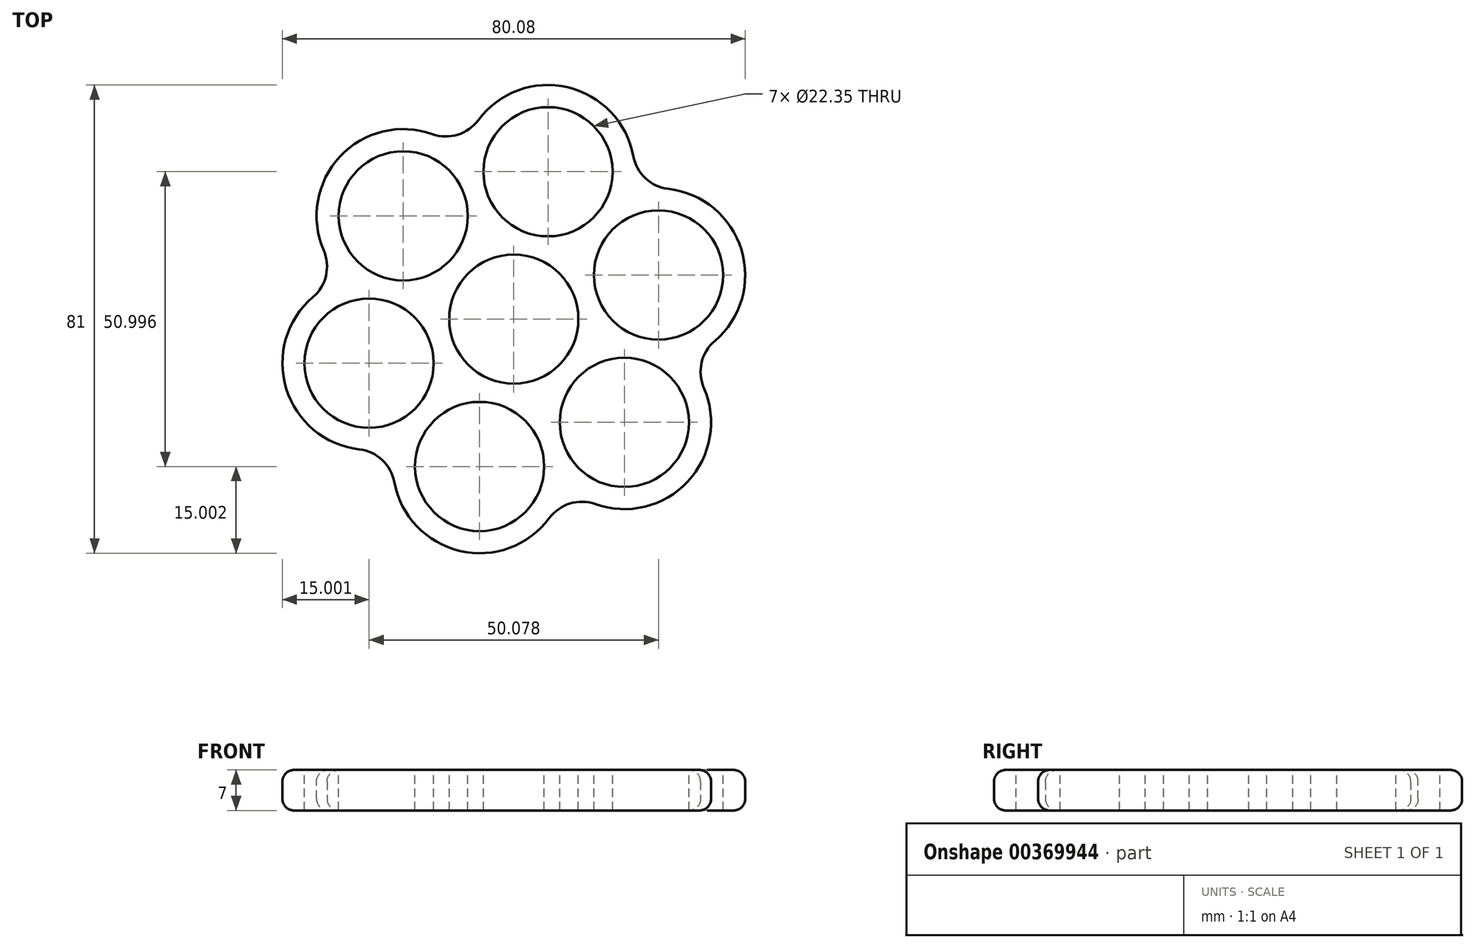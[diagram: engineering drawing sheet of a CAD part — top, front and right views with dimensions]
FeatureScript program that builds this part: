
annotation { "Feature Type Name" : "Feature", "Feature Type Description" : "" }
export const myFeature = defineFeature(function(context is Context, id is Id, definition is map)
    precondition{}
    {
        {
            var Q0;
            Q0=qCreatedBy(makeId("Top.planeOp"),FACE);
            var sketch = newSketch(context, id + "F0", { "sketchPlane" : qUnion([Q0])});
            skCircle(sketch, "E0", {"center": v(0, 0) * mm, "radius": 11.18 * mm});
            skLineSegment(sketch, "E1", {"start": v(0, 0) * mm, "end": v(-19.13, 17.87) * mm});
            skLineSegment(sketch, "E2", {"start": v(0, 0) * mm, "end": v(25.04, 7.63) * mm});
            skLineSegment(sketch, "E3", {"start": v(0, 0) * mm, "end": v(-5.91, -25.5) * mm});
            skCircle(sketch, "E4", {"center": v(-19.13, 17.87) * mm, "radius": 11.18 * mm});
            skCircle(sketch, "E5", {"center": v(25.04, 7.63) * mm, "radius": 11.18 * mm});
            skCircle(sketch, "E6", {"center": v(-5.91, -25.5) * mm, "radius": 11.18 * mm});
            skCircle(sketch, "E7", {"center": v(0, 0) * mm, "radius": 15 * mm});
            skCircle(sketch, "E8", {"center": v(-19.13, 17.87) * mm, "radius": 15 * mm});
            skCircle(sketch, "E9", {"center": v(25.04, 7.63) * mm, "radius": 15 * mm});
            skCircle(sketch, "E10", {"center": v(-5.91, -25.5) * mm, "radius": 15 * mm});
            skLineSegment(sketch, "E11", {"start": v(-19.13, 17.87) * mm, "end": v(-8.88, 28.83) * mm});
            skLineSegment(sketch, "E12", {"start": v(25.04, 7.63) * mm, "end": v(20.67, 21.98) * mm});
            skLineSegment(sketch, "E13", {"start": v(-5.91, -25.5) * mm, "end": v(8.7, -28.89) * mm});
            skLineSegment(sketch, "E14", {"start": v(-5.91, -25.5) * mm, "end": v(-20.53, -22.1) * mm});
            skLineSegment(sketch, "E15", {"start": v(-19.13, 17.87) * mm, "end": v(-29.37, 6.91) * mm});
            skLineSegment(sketch, "E16", {"start": v(25.04, 7.63) * mm, "end": v(29.41, -6.72) * mm});
            skLineSegment(sketch, "E17", {"start": v(0, 0) * mm, "end": v(5.91, 25.5) * mm});
            skLineSegment(sketch, "E18", {"start": v(0, 0) * mm, "end": v(19.13, -17.87) * mm});
            skLineSegment(sketch, "E19", {"start": v(0, 0) * mm, "end": v(-25.04, -7.63) * mm});
            skCircle(sketch, "E20", {"center": v(-25.04, -7.63) * mm, "radius": 11.18 * mm});
            skCircle(sketch, "E21", {"center": v(5.91, 25.5) * mm, "radius": 11.18 * mm});
            skCircle(sketch, "E22", {"center": v(19.13, -17.87) * mm, "radius": 11.18 * mm});
            skCircle(sketch, "E23", {"center": v(-25.04, -7.63) * mm, "radius": 15 * mm});
            skCircle(sketch, "E24", {"center": v(5.91, 25.5) * mm, "radius": 15 * mm});
            skCircle(sketch, "E25", {"center": v(19.13, -17.87) * mm, "radius": 15 * mm});
            skSolve(sketch);
        }
        {
            var Q0;
            {var subQ0=sQuery(id+"F0.wireOp",EDGE,"E11");var subQ1=sQuery(id+"F0.wireOp",EDGE,"E4");var subQ2=makeQuery(id+"F0.imprint","INTERSECT",VERTEX,{"derivedFrom":[subQ1,subQ0]});Q0=makeQuery(id+"F0.imprint","IMPRINT",FACE,{"disambiguationData":[TD([[makeQuery(id+"F0.imprint","IMPRINT",EDGE,{"disambiguationData":[TD([[subQ2,1.0]])],"derivedFrom":subQ1}),-1.0]])]});}
            var Q1;
            {var subQ0=sQuery(id+"F0.wireOp",EDGE,"E11");var subQ1=sQuery(id+"F0.wireOp",EDGE,"E4");var subQ2=makeQuery(id+"F0.imprint","INTERSECT",VERTEX,{"derivedFrom":[subQ1,subQ0]});Q1=makeQuery(id+"F0.imprint","IMPRINT",FACE,{"disambiguationData":[TD([[makeQuery(id+"F0.imprint","IMPRINT",EDGE,{"disambiguationData":[TD([[subQ2,-1.0]])],"derivedFrom":subQ1}),-1.0]])]});}
            var Q2;
            {var subQ0=sQuery(id+"F0.wireOp",EDGE,"E15");var subQ1=sQuery(id+"F0.wireOp",EDGE,"E4");var subQ2=makeQuery(id+"F0.imprint","INTERSECT",VERTEX,{"derivedFrom":[subQ1,subQ0]});Q2=makeQuery(id+"F0.imprint","IMPRINT",FACE,{"disambiguationData":[TD([[makeQuery(id+"F0.imprint","IMPRINT",EDGE,{"disambiguationData":[TD([[subQ2,-1.0]])],"derivedFrom":subQ1}),-1.0]])]});}
            var Q3;
            {var subQ0=sQuery(id+"F0.wireOp",EDGE,"E24");var subQ1=sQuery(id+"F0.wireOp",EDGE,"E5");var subQ2=makeQuery(id+"F0.imprint","INTERSECT",VERTEX,{"derivedFrom":[subQ1,subQ0]});Q3=makeQuery(id+"F0.imprint","IMPRINT",FACE,{"disambiguationData":[TD([[makeQuery(id+"F0.imprint","IMPRINT",EDGE,{"disambiguationData":[TD([[subQ2,1.0]])],"derivedFrom":subQ1}),-1.0]])]});}
            var Q4;
            {var subQ0=sQuery(id+"F0.wireOp",EDGE,"E25");var subQ1=sQuery(id+"F0.wireOp",EDGE,"E5");var subQ2=makeQuery(id+"F0.imprint","INTERSECT",VERTEX,{"derivedFrom":[subQ1,subQ0]});Q4=makeQuery(id+"F0.imprint","IMPRINT",FACE,{"disambiguationData":[TD([[makeQuery(id+"F0.imprint","IMPRINT",EDGE,{"disambiguationData":[TD([[subQ2,-1.0]])],"derivedFrom":subQ1}),-1.0]])]});}
            var Q5;
            {var subQ0=sQuery(id+"F0.wireOp",EDGE,"E12");var subQ1=sQuery(id+"F0.wireOp",EDGE,"E5");var subQ2=makeQuery(id+"F0.imprint","INTERSECT",VERTEX,{"derivedFrom":[subQ1,subQ0]});Q5=makeQuery(id+"F0.imprint","IMPRINT",FACE,{"disambiguationData":[TD([[makeQuery(id+"F0.imprint","IMPRINT",EDGE,{"disambiguationData":[TD([[subQ2,1.0]])],"derivedFrom":subQ1}),-1.0]])]});}
            var Q6;
            {var subQ0=sQuery(id+"F0.wireOp",EDGE,"E23");var subQ1=sQuery(id+"F0.wireOp",EDGE,"E6");var subQ2=makeQuery(id+"F0.imprint","INTERSECT",VERTEX,{"derivedFrom":[subQ1,subQ0]});Q6=makeQuery(id+"F0.imprint","IMPRINT",FACE,{"disambiguationData":[TD([[makeQuery(id+"F0.imprint","IMPRINT",EDGE,{"disambiguationData":[TD([[subQ2,-1.0]])],"derivedFrom":subQ1}),-1.0]])]});}
            var Q7;
            {var subQ0=sQuery(id+"F0.wireOp",EDGE,"E14");var subQ1=sQuery(id+"F0.wireOp",EDGE,"E6");var subQ2=makeQuery(id+"F0.imprint","INTERSECT",VERTEX,{"derivedFrom":[subQ1,subQ0]});Q7=makeQuery(id+"F0.imprint","IMPRINT",FACE,{"disambiguationData":[TD([[makeQuery(id+"F0.imprint","IMPRINT",EDGE,{"disambiguationData":[TD([[subQ2,-1.0]])],"derivedFrom":subQ1}),-1.0]])]});}
            var Q8;
            {var subQ0=sQuery(id+"F0.wireOp",EDGE,"E25");var subQ1=sQuery(id+"F0.wireOp",EDGE,"E6");var subQ2=makeQuery(id+"F0.imprint","INTERSECT",VERTEX,{"derivedFrom":[subQ1,subQ0]});Q8=makeQuery(id+"F0.imprint","IMPRINT",FACE,{"disambiguationData":[TD([[makeQuery(id+"F0.imprint","IMPRINT",EDGE,{"disambiguationData":[TD([[subQ2,1.0]])],"derivedFrom":subQ1}),-1.0]])]});}
            var Q9;
            {var subQ0=sQuery(id+"F0.wireOp",EDGE,"E24");var subQ1=sQuery(id+"F0.wireOp",EDGE,"E8");var subQ2=makeQuery(id+"F0.imprint","INTERSECT",VERTEX,{"disambiguationData":[OD(0.0)],"derivedFrom":[subQ1,subQ0]});Q9=makeQuery(id+"F0.imprint","IMPRINT",FACE,{"disambiguationData":[TD([[makeQuery(id+"F0.imprint","IMPRINT",EDGE,{"disambiguationData":[TD([[subQ2,1.0]])],"derivedFrom":subQ1}),-1.0]])]});}
            var Q10;
            {var subQ0=sQuery(id+"F0.wireOp",EDGE,"E23");var subQ1=sQuery(id+"F0.wireOp",EDGE,"E8");var subQ2=makeQuery(id+"F0.imprint","INTERSECT",VERTEX,{"disambiguationData":[OD(0.0)],"derivedFrom":[subQ1,subQ0]});Q10=makeQuery(id+"F0.imprint","IMPRINT",FACE,{"disambiguationData":[TD([[makeQuery(id+"F0.imprint","IMPRINT",EDGE,{"disambiguationData":[TD([[subQ2,-1.0]])],"derivedFrom":subQ1}),-1.0]])]});}
            var Q11;
            {var subQ0=sQuery(id+"F0.wireOp",EDGE,"E25");var subQ1=sQuery(id+"F0.wireOp",EDGE,"E9");var subQ2=makeQuery(id+"F0.imprint","INTERSECT",VERTEX,{"disambiguationData":[OD(0.0)],"derivedFrom":[subQ1,subQ0]});Q11=makeQuery(id+"F0.imprint","IMPRINT",FACE,{"disambiguationData":[TD([[makeQuery(id+"F0.imprint","IMPRINT",EDGE,{"disambiguationData":[TD([[subQ2,1.0]])],"derivedFrom":subQ1}),-1.0]])]});}
            var Q12;
            {var subQ0=sQuery(id+"F0.wireOp",EDGE,"E24");var subQ1=sQuery(id+"F0.wireOp",EDGE,"E8");var subQ2=makeQuery(id+"F0.imprint","INTERSECT",VERTEX,{"disambiguationData":[OD(0.0)],"derivedFrom":[subQ1,subQ0]});Q12=makeQuery(id+"F0.imprint","IMPRINT",FACE,{"disambiguationData":[TD([[makeQuery(id+"F0.imprint","IMPRINT",EDGE,{"disambiguationData":[TD([[subQ2,1.0]])],"derivedFrom":subQ1}),1.0]])]});}
            var Q13;
            {var subQ0=sQuery(id+"F0.wireOp",EDGE,"E23");var subQ1=sQuery(id+"F0.wireOp",EDGE,"E8");var subQ2=makeQuery(id+"F0.imprint","INTERSECT",VERTEX,{"disambiguationData":[OD(0.0)],"derivedFrom":[subQ1,subQ0]});Q13=makeQuery(id+"F0.imprint","IMPRINT",FACE,{"disambiguationData":[TD([[makeQuery(id+"F0.imprint","IMPRINT",EDGE,{"disambiguationData":[TD([[subQ2,-1.0]])],"derivedFrom":subQ1}),1.0]])]});}
            var Q14;
            {var subQ0=sQuery(id+"F0.wireOp",EDGE,"E24");var subQ1=sQuery(id+"F0.wireOp",EDGE,"E9");var subQ2=makeQuery(id+"F0.imprint","INTERSECT",VERTEX,{"disambiguationData":[OD(0.0)],"derivedFrom":[subQ1,subQ0]});Q14=makeQuery(id+"F0.imprint","IMPRINT",FACE,{"disambiguationData":[TD([[makeQuery(id+"F0.imprint","IMPRINT",EDGE,{"disambiguationData":[TD([[subQ2,-1.0]])],"derivedFrom":subQ1}),1.0]])]});}
            var Q15;
            {var subQ0=sQuery(id+"F0.wireOp",EDGE,"E25");var subQ1=sQuery(id+"F0.wireOp",EDGE,"E9");var subQ2=makeQuery(id+"F0.imprint","INTERSECT",VERTEX,{"disambiguationData":[OD(1.0)],"derivedFrom":[subQ1,subQ0]});Q15=makeQuery(id+"F0.imprint","IMPRINT",FACE,{"disambiguationData":[TD([[makeQuery(id+"F0.imprint","IMPRINT",EDGE,{"disambiguationData":[TD([[subQ2,-1.0]])],"derivedFrom":subQ1}),1.0]])]});}
            var Q16;
            {var subQ0=sQuery(id+"F0.wireOp",EDGE,"E25");var subQ1=sQuery(id+"F0.wireOp",EDGE,"E10");var subQ2=makeQuery(id+"F0.imprint","INTERSECT",VERTEX,{"disambiguationData":[OD(1.0)],"derivedFrom":[subQ1,subQ0]});Q16=makeQuery(id+"F0.imprint","IMPRINT",FACE,{"disambiguationData":[TD([[makeQuery(id+"F0.imprint","IMPRINT",EDGE,{"disambiguationData":[TD([[subQ2,1.0]])],"derivedFrom":subQ1}),1.0]])]});}
            var Q17;
            {var subQ0=sQuery(id+"F0.wireOp",EDGE,"E23");var subQ1=sQuery(id+"F0.wireOp",EDGE,"E10");var subQ2=makeQuery(id+"F0.imprint","INTERSECT",VERTEX,{"disambiguationData":[OD(1.0)],"derivedFrom":[subQ1,subQ0]});Q17=makeQuery(id+"F0.imprint","IMPRINT",FACE,{"disambiguationData":[TD([[makeQuery(id+"F0.imprint","IMPRINT",EDGE,{"disambiguationData":[TD([[subQ2,-1.0]])],"derivedFrom":subQ1}),1.0]])]});}
            var Q18;
            {var subQ3=sQuery(id+"F0.wireOp",EDGE,"E7");var subQ5=sQuery(id+"F0.wireOp",EDGE,"E8");var subQ6=makeQuery(id+"F0.imprint","INTERSECT",VERTEX,{"disambiguationData":[OD(0.0)],"derivedFrom":[subQ3,subQ5]});Q18=makeQuery(id+"F0.imprint","IMPRINT",FACE,{"disambiguationData":[TD([[makeQuery(id+"F0.imprint","IMPRINT",EDGE,{"disambiguationData":[TD([[subQ6,-1.0]])],"derivedFrom":subQ5}),1.0]])]});}
            var Q19;
            {var subQ0=sQuery(id+"F0.wireOp",EDGE,"E8");var subQ3=sQuery(id+"F0.wireOp",EDGE,"E7");var subQ5=makeQuery(id+"F0.imprint","INTERSECT",VERTEX,{"disambiguationData":[OD(1.0)],"derivedFrom":[subQ3,subQ0]});Q19=makeQuery(id+"F0.imprint","IMPRINT",FACE,{"disambiguationData":[TD([[makeQuery(id+"F0.imprint","IMPRINT",EDGE,{"disambiguationData":[TD([[subQ5,1.0]])],"derivedFrom":subQ3}),1.0]])]});}
            var Q20;
            {var subQ3=sQuery(id+"F0.wireOp",EDGE,"E7");var subQ5=sQuery(id+"F0.wireOp",EDGE,"E8");var subQ6=makeQuery(id+"F0.imprint","INTERSECT",VERTEX,{"disambiguationData":[OD(1.0)],"derivedFrom":[subQ3,subQ5]});Q20=makeQuery(id+"F0.imprint","IMPRINT",FACE,{"disambiguationData":[TD([[makeQuery(id+"F0.imprint","IMPRINT",EDGE,{"disambiguationData":[TD([[subQ6,1.0]])],"derivedFrom":subQ5}),1.0]])]});}
            var Q21;
            {var subQ0=sQuery(id+"F0.wireOp",EDGE,"E8");var subQ3=sQuery(id+"F0.wireOp",EDGE,"E7");var subQ5=makeQuery(id+"F0.imprint","INTERSECT",VERTEX,{"disambiguationData":[OD(0.0)],"derivedFrom":[subQ3,subQ0]});Q21=makeQuery(id+"F0.imprint","IMPRINT",FACE,{"disambiguationData":[TD([[makeQuery(id+"F0.imprint","IMPRINT",EDGE,{"disambiguationData":[TD([[subQ5,-1.0]])],"derivedFrom":subQ3}),1.0]])]});}
            var Q22;
            {var subQ3=sQuery(id+"F0.wireOp",EDGE,"E21");var subQ5=sQuery(id+"F0.wireOp",EDGE,"E8");var subQ6=makeQuery(id+"F0.imprint","INTERSECT",VERTEX,{"derivedFrom":[subQ5,subQ3]});Q22=makeQuery(id+"F0.imprint","IMPRINT",FACE,{"disambiguationData":[TD([[makeQuery(id+"F0.imprint","IMPRINT",EDGE,{"disambiguationData":[TD([[subQ6,1.0]])],"derivedFrom":subQ5}),-1.0]])]});}
            var Q23;
            {var subQ0=sQuery(id+"F0.wireOp",EDGE,"E24");var subQ1=sQuery(id+"F0.wireOp",EDGE,"E7");var subQ2=makeQuery(id+"F0.imprint","INTERSECT",VERTEX,{"disambiguationData":[OD(1.0)],"derivedFrom":[subQ1,subQ0]});Q23=makeQuery(id+"F0.imprint","IMPRINT",FACE,{"disambiguationData":[TD([[makeQuery(id+"F0.imprint","IMPRINT",EDGE,{"disambiguationData":[TD([[subQ2,1.0]])],"derivedFrom":subQ1}),1.0]])]});}
            var Q24;
            {var subQ0=sQuery(id+"F0.wireOp",EDGE,"E24");var subQ1=sQuery(id+"F0.wireOp",EDGE,"E7");var subQ2=makeQuery(id+"F0.imprint","INTERSECT",VERTEX,{"disambiguationData":[OD(0.0)],"derivedFrom":[subQ1,subQ0]});Q24=makeQuery(id+"F0.imprint","IMPRINT",FACE,{"disambiguationData":[TD([[makeQuery(id+"F0.imprint","IMPRINT",EDGE,{"disambiguationData":[TD([[subQ2,-1.0]])],"derivedFrom":subQ1}),1.0]])]});}
            var Q25;
            {var subQ3=sQuery(id+"F0.wireOp",EDGE,"E21");var subQ5=sQuery(id+"F0.wireOp",EDGE,"E9");var subQ7=makeQuery(id+"F0.imprint","INTERSECT",VERTEX,{"derivedFrom":[subQ5,subQ3]});Q25=makeQuery(id+"F0.imprint","IMPRINT",FACE,{"disambiguationData":[TD([[makeQuery(id+"F0.imprint","IMPRINT",EDGE,{"disambiguationData":[TD([[subQ7,-1.0]])],"derivedFrom":subQ5}),-1.0]])]});}
            var Q26;
            {var subQ3=sQuery(id+"F0.wireOp",EDGE,"E7");var subQ5=sQuery(id+"F0.wireOp",EDGE,"E9");var subQ6=makeQuery(id+"F0.imprint","INTERSECT",VERTEX,{"disambiguationData":[OD(0.0)],"derivedFrom":[subQ3,subQ5]});Q26=makeQuery(id+"F0.imprint","IMPRINT",FACE,{"disambiguationData":[TD([[makeQuery(id+"F0.imprint","IMPRINT",EDGE,{"disambiguationData":[TD([[subQ6,1.0]])],"derivedFrom":subQ5}),1.0]])]});}
            var Q27;
            {var subQ0=sQuery(id+"F0.wireOp",EDGE,"E9");var subQ3=sQuery(id+"F0.wireOp",EDGE,"E7");var subQ5=makeQuery(id+"F0.imprint","INTERSECT",VERTEX,{"disambiguationData":[OD(0.0)],"derivedFrom":[subQ3,subQ0]});Q27=makeQuery(id+"F0.imprint","IMPRINT",FACE,{"disambiguationData":[TD([[makeQuery(id+"F0.imprint","IMPRINT",EDGE,{"disambiguationData":[TD([[subQ5,1.0]])],"derivedFrom":subQ3}),1.0]])]});}
            var Q28;
            {var subQ0=sQuery(id+"F0.wireOp",EDGE,"E9");var subQ3=sQuery(id+"F0.wireOp",EDGE,"E7");var subQ5=makeQuery(id+"F0.imprint","INTERSECT",VERTEX,{"disambiguationData":[OD(1.0)],"derivedFrom":[subQ3,subQ0]});Q28=makeQuery(id+"F0.imprint","IMPRINT",FACE,{"disambiguationData":[TD([[makeQuery(id+"F0.imprint","IMPRINT",EDGE,{"disambiguationData":[TD([[subQ5,-1.0]])],"derivedFrom":subQ3}),1.0]])]});}
            var Q29;
            {var subQ3=sQuery(id+"F0.wireOp",EDGE,"E7");var subQ5=sQuery(id+"F0.wireOp",EDGE,"E9");var subQ6=makeQuery(id+"F0.imprint","INTERSECT",VERTEX,{"disambiguationData":[OD(1.0)],"derivedFrom":[subQ3,subQ5]});Q29=makeQuery(id+"F0.imprint","IMPRINT",FACE,{"disambiguationData":[TD([[makeQuery(id+"F0.imprint","IMPRINT",EDGE,{"disambiguationData":[TD([[subQ6,-1.0]])],"derivedFrom":subQ5}),1.0]])]});}
            var Q30;
            {var subQ0=sQuery(id+"F0.wireOp",EDGE,"E8");var subQ5=sQuery(id+"F0.wireOp",EDGE,"E7");var subQ6=makeQuery(id+"F0.imprint","INTERSECT",VERTEX,{"disambiguationData":[OD(1.0)],"derivedFrom":[subQ5,subQ0]});Q30=makeQuery(id+"F0.imprint","IMPRINT",FACE,{"disambiguationData":[TD([[makeQuery(id+"F0.imprint","IMPRINT",EDGE,{"disambiguationData":[TD([[subQ6,-1.0]])],"derivedFrom":subQ5}),1.0]])]});}
            var Q31;
            {var subQ3=sQuery(id+"F0.wireOp",EDGE,"E20");var subQ5=sQuery(id+"F0.wireOp",EDGE,"E8");var subQ6=makeQuery(id+"F0.imprint","INTERSECT",VERTEX,{"derivedFrom":[subQ5,subQ3]});Q31=makeQuery(id+"F0.imprint","IMPRINT",FACE,{"disambiguationData":[TD([[makeQuery(id+"F0.imprint","IMPRINT",EDGE,{"disambiguationData":[TD([[subQ6,-1.0]])],"derivedFrom":subQ5}),-1.0]])]});}
            var Q32;
            {var subQ0=sQuery(id+"F0.wireOp",EDGE,"E23");var subQ1=sQuery(id+"F0.wireOp",EDGE,"E7");var subQ2=makeQuery(id+"F0.imprint","INTERSECT",VERTEX,{"disambiguationData":[OD(0.0)],"derivedFrom":[subQ1,subQ0]});Q32=makeQuery(id+"F0.imprint","IMPRINT",FACE,{"disambiguationData":[TD([[makeQuery(id+"F0.imprint","IMPRINT",EDGE,{"disambiguationData":[TD([[subQ2,-1.0]])],"derivedFrom":subQ1}),1.0]])]});}
            var Q33;
            {var subQ0=sQuery(id+"F0.wireOp",EDGE,"E23");var subQ1=sQuery(id+"F0.wireOp",EDGE,"E7");var subQ2=makeQuery(id+"F0.imprint","INTERSECT",VERTEX,{"disambiguationData":[OD(1.0)],"derivedFrom":[subQ1,subQ0]});Q33=makeQuery(id+"F0.imprint","IMPRINT",FACE,{"disambiguationData":[TD([[makeQuery(id+"F0.imprint","IMPRINT",EDGE,{"disambiguationData":[TD([[subQ2,1.0]])],"derivedFrom":subQ1}),1.0]])]});}
            var Q34;
            {var subQ0=sQuery(id+"F0.wireOp",EDGE,"E23");var subQ5=sQuery(id+"F0.wireOp",EDGE,"E10");var subQ6=makeQuery(id+"F0.imprint","INTERSECT",VERTEX,{"disambiguationData":[OD(1.0)],"derivedFrom":[subQ5,subQ0]});Q34=makeQuery(id+"F0.imprint","IMPRINT",FACE,{"disambiguationData":[TD([[makeQuery(id+"F0.imprint","IMPRINT",EDGE,{"disambiguationData":[TD([[subQ6,-1.0]])],"derivedFrom":subQ5}),-1.0]])]});}
            var Q35;
            {var subQ0=sQuery(id+"F0.wireOp",EDGE,"E23");var subQ5=sQuery(id+"F0.wireOp",EDGE,"E7");var subQ7=makeQuery(id+"F0.imprint","INTERSECT",VERTEX,{"disambiguationData":[OD(1.0)],"derivedFrom":[subQ5,subQ0]});Q35=makeQuery(id+"F0.imprint","IMPRINT",FACE,{"disambiguationData":[TD([[makeQuery(id+"F0.imprint","IMPRINT",EDGE,{"disambiguationData":[TD([[subQ7,-1.0]])],"derivedFrom":subQ5}),1.0]])]});}
            var Q36;
            {var subQ0=sQuery(id+"F0.wireOp",EDGE,"E10");var subQ3=sQuery(id+"F0.wireOp",EDGE,"E7");var subQ5=makeQuery(id+"F0.imprint","INTERSECT",VERTEX,{"disambiguationData":[OD(0.0)],"derivedFrom":[subQ3,subQ0]});Q36=makeQuery(id+"F0.imprint","IMPRINT",FACE,{"disambiguationData":[TD([[makeQuery(id+"F0.imprint","IMPRINT",EDGE,{"disambiguationData":[TD([[subQ5,-1.0]])],"derivedFrom":subQ3}),1.0]])]});}
            var Q37;
            {var subQ3=sQuery(id+"F0.wireOp",EDGE,"E7");var subQ5=sQuery(id+"F0.wireOp",EDGE,"E10");var subQ6=makeQuery(id+"F0.imprint","INTERSECT",VERTEX,{"disambiguationData":[OD(0.0)],"derivedFrom":[subQ3,subQ5]});Q37=makeQuery(id+"F0.imprint","IMPRINT",FACE,{"disambiguationData":[TD([[makeQuery(id+"F0.imprint","IMPRINT",EDGE,{"disambiguationData":[TD([[subQ6,-1.0]])],"derivedFrom":subQ5}),1.0]])]});}
            var Q38;
            {var subQ0=sQuery(id+"F0.wireOp",EDGE,"E10");var subQ3=sQuery(id+"F0.wireOp",EDGE,"E7");var subQ5=makeQuery(id+"F0.imprint","INTERSECT",VERTEX,{"disambiguationData":[OD(1.0)],"derivedFrom":[subQ3,subQ0]});Q38=makeQuery(id+"F0.imprint","IMPRINT",FACE,{"disambiguationData":[TD([[makeQuery(id+"F0.imprint","IMPRINT",EDGE,{"disambiguationData":[TD([[subQ5,1.0]])],"derivedFrom":subQ3}),1.0]])]});}
            var Q39;
            {var subQ3=sQuery(id+"F0.wireOp",EDGE,"E7");var subQ5=sQuery(id+"F0.wireOp",EDGE,"E10");var subQ6=makeQuery(id+"F0.imprint","INTERSECT",VERTEX,{"disambiguationData":[OD(1.0)],"derivedFrom":[subQ3,subQ5]});Q39=makeQuery(id+"F0.imprint","IMPRINT",FACE,{"disambiguationData":[TD([[makeQuery(id+"F0.imprint","IMPRINT",EDGE,{"disambiguationData":[TD([[subQ6,1.0]])],"derivedFrom":subQ5}),1.0]])]});}
            var Q40;
            {var subQ0=sQuery(id+"F0.wireOp",EDGE,"E10");var subQ5=sQuery(id+"F0.wireOp",EDGE,"E7");var subQ6=makeQuery(id+"F0.imprint","INTERSECT",VERTEX,{"disambiguationData":[OD(1.0)],"derivedFrom":[subQ5,subQ0]});Q40=makeQuery(id+"F0.imprint","IMPRINT",FACE,{"disambiguationData":[TD([[makeQuery(id+"F0.imprint","IMPRINT",EDGE,{"disambiguationData":[TD([[subQ6,-1.0]])],"derivedFrom":subQ5}),1.0]])]});}
            var Q41;
            {var subQ3=sQuery(id+"F0.wireOp",EDGE,"E25");var subQ5=sQuery(id+"F0.wireOp",EDGE,"E7");var subQ6=makeQuery(id+"F0.imprint","INTERSECT",VERTEX,{"disambiguationData":[OD(1.0)],"derivedFrom":[subQ5,subQ3]});Q41=makeQuery(id+"F0.imprint","IMPRINT",FACE,{"disambiguationData":[TD([[makeQuery(id+"F0.imprint","IMPRINT",EDGE,{"disambiguationData":[TD([[subQ6,-1.0]])],"derivedFrom":subQ5}),1.0]])]});}
            var Q42;
            {var subQ0=sQuery(id+"F0.wireOp",EDGE,"E25");var subQ5=sQuery(id+"F0.wireOp",EDGE,"E9");var subQ7=makeQuery(id+"F0.imprint","INTERSECT",VERTEX,{"disambiguationData":[OD(1.0)],"derivedFrom":[subQ5,subQ0]});Q42=makeQuery(id+"F0.imprint","IMPRINT",FACE,{"disambiguationData":[TD([[makeQuery(id+"F0.imprint","IMPRINT",EDGE,{"disambiguationData":[TD([[subQ7,-1.0]])],"derivedFrom":subQ5}),-1.0]])]});}
            var Q43;
            {var subQ0=sQuery(id+"F0.wireOp",EDGE,"E25");var subQ1=sQuery(id+"F0.wireOp",EDGE,"E7");var subQ2=makeQuery(id+"F0.imprint","INTERSECT",VERTEX,{"disambiguationData":[OD(1.0)],"derivedFrom":[subQ1,subQ0]});Q43=makeQuery(id+"F0.imprint","IMPRINT",FACE,{"disambiguationData":[TD([[makeQuery(id+"F0.imprint","IMPRINT",EDGE,{"disambiguationData":[TD([[subQ2,1.0]])],"derivedFrom":subQ1}),1.0]])]});}
            var Q44;
            {var subQ0=sQuery(id+"F0.wireOp",EDGE,"E25");var subQ1=sQuery(id+"F0.wireOp",EDGE,"E7");var subQ2=makeQuery(id+"F0.imprint","INTERSECT",VERTEX,{"disambiguationData":[OD(0.0)],"derivedFrom":[subQ1,subQ0]});Q44=makeQuery(id+"F0.imprint","IMPRINT",FACE,{"disambiguationData":[TD([[makeQuery(id+"F0.imprint","IMPRINT",EDGE,{"disambiguationData":[TD([[subQ2,-1.0]])],"derivedFrom":subQ1}),1.0]])]});}
            var Q45;
            {var subQ0=sQuery(id+"F0.wireOp",EDGE,"E25");var subQ5=sQuery(id+"F0.wireOp",EDGE,"E10");var subQ6=makeQuery(id+"F0.imprint","INTERSECT",VERTEX,{"disambiguationData":[OD(1.0)],"derivedFrom":[subQ5,subQ0]});Q45=makeQuery(id+"F0.imprint","IMPRINT",FACE,{"disambiguationData":[TD([[makeQuery(id+"F0.imprint","IMPRINT",EDGE,{"disambiguationData":[TD([[subQ6,1.0]])],"derivedFrom":subQ5}),-1.0]])]});}
            var Q46;
            {var subQ0=sQuery(id+"F0.wireOp",EDGE,"E24");var subQ5=sQuery(id+"F0.wireOp",EDGE,"E7");var subQ7=makeQuery(id+"F0.imprint","INTERSECT",VERTEX,{"disambiguationData":[OD(1.0)],"derivedFrom":[subQ5,subQ0]});Q46=makeQuery(id+"F0.imprint","IMPRINT",FACE,{"disambiguationData":[TD([[makeQuery(id+"F0.imprint","IMPRINT",EDGE,{"disambiguationData":[TD([[subQ7,-1.0]])],"derivedFrom":subQ5}),1.0]])]});}
            var Q47;
            {var subQ3=sQuery(id+"F0.wireOp",EDGE,"E9");var subQ5=sQuery(id+"F0.wireOp",EDGE,"E7");var subQ6=makeQuery(id+"F0.imprint","INTERSECT",VERTEX,{"disambiguationData":[OD(0.0)],"derivedFrom":[subQ5,subQ3]});Q47=makeQuery(id+"F0.imprint","IMPRINT",FACE,{"disambiguationData":[TD([[makeQuery(id+"F0.imprint","IMPRINT",EDGE,{"disambiguationData":[TD([[subQ6,-1.0]])],"derivedFrom":subQ5}),1.0]])]});}
            var Q48;
            {var subQ0=sQuery(id+"F0.wireOp",EDGE,"E10");var subQ1=sQuery(id+"F0.wireOp",EDGE,"E7");var subQ2=makeQuery(id+"F0.imprint","INTERSECT",VERTEX,{"disambiguationData":[OD(1.0)],"derivedFrom":[subQ1,subQ0]});Q48=makeQuery(id+"F0.imprint","IMPRINT",FACE,{"disambiguationData":[TD([[makeQuery(id+"F0.imprint","IMPRINT",EDGE,{"disambiguationData":[TD([[subQ2,-1.0]])],"derivedFrom":subQ1}),-1.0]])]});}
            var Q49;
            {var subQ0=sQuery(id+"F0.wireOp",EDGE,"E23");var subQ1=sQuery(id+"F0.wireOp",EDGE,"E7");var subQ2=makeQuery(id+"F0.imprint","INTERSECT",VERTEX,{"disambiguationData":[OD(1.0)],"derivedFrom":[subQ1,subQ0]});Q49=makeQuery(id+"F0.imprint","IMPRINT",FACE,{"disambiguationData":[TD([[makeQuery(id+"F0.imprint","IMPRINT",EDGE,{"disambiguationData":[TD([[subQ2,-1.0]])],"derivedFrom":subQ1}),-1.0]])]});}
            var Q50;
            {var subQ0=sQuery(id+"F0.wireOp",EDGE,"E8");var subQ1=sQuery(id+"F0.wireOp",EDGE,"E7");var subQ2=makeQuery(id+"F0.imprint","INTERSECT",VERTEX,{"disambiguationData":[OD(1.0)],"derivedFrom":[subQ1,subQ0]});Q50=makeQuery(id+"F0.imprint","IMPRINT",FACE,{"disambiguationData":[TD([[makeQuery(id+"F0.imprint","IMPRINT",EDGE,{"disambiguationData":[TD([[subQ2,-1.0]])],"derivedFrom":subQ1}),-1.0]])]});}
            var Q51;
            {var subQ0=sQuery(id+"F0.wireOp",EDGE,"E24");var subQ1=sQuery(id+"F0.wireOp",EDGE,"E7");var subQ2=makeQuery(id+"F0.imprint","INTERSECT",VERTEX,{"disambiguationData":[OD(1.0)],"derivedFrom":[subQ1,subQ0]});Q51=makeQuery(id+"F0.imprint","IMPRINT",FACE,{"disambiguationData":[TD([[makeQuery(id+"F0.imprint","IMPRINT",EDGE,{"disambiguationData":[TD([[subQ2,-1.0]])],"derivedFrom":subQ1}),-1.0]])]});}
            var Q52;
            {var subQ0=sQuery(id+"F0.wireOp",EDGE,"E9");var subQ1=sQuery(id+"F0.wireOp",EDGE,"E7");var subQ2=makeQuery(id+"F0.imprint","INTERSECT",VERTEX,{"disambiguationData":[OD(0.0)],"derivedFrom":[subQ1,subQ0]});Q52=makeQuery(id+"F0.imprint","IMPRINT",FACE,{"disambiguationData":[TD([[makeQuery(id+"F0.imprint","IMPRINT",EDGE,{"disambiguationData":[TD([[subQ2,-1.0]])],"derivedFrom":subQ1}),-1.0]])]});}
            var Q53;
            {var subQ0=sQuery(id+"F0.wireOp",EDGE,"E25");var subQ1=sQuery(id+"F0.wireOp",EDGE,"E7");var subQ2=makeQuery(id+"F0.imprint","INTERSECT",VERTEX,{"disambiguationData":[OD(1.0)],"derivedFrom":[subQ1,subQ0]});Q53=makeQuery(id+"F0.imprint","IMPRINT",FACE,{"disambiguationData":[TD([[makeQuery(id+"F0.imprint","IMPRINT",EDGE,{"disambiguationData":[TD([[subQ2,-1.0]])],"derivedFrom":subQ1}),-1.0]])]});}
            extrude(context, id + "F1", {"entities" : qUnion([Q0, Q1, Q2, Q3, Q4, Q5, Q6, Q7, Q8, Q9, Q10, Q11, Q12, Q13, Q14, Q15, Q16, Q17, Q18, Q19, Q20, Q21, Q22, Q23, Q24, Q25, Q26, Q27, Q28, Q29, Q30, Q31, Q32, Q33, Q34, Q35, Q36, Q37, Q38, Q39, Q40, Q41, Q42, Q43, Q44, Q45, Q46, Q47, Q48, Q49, Q50, Q51, Q52, Q53]), "oppositeDirection" : true, "depth" : 7 * mm, "offsetDistance" : 25 * mm});
        }
        {
            var Q0;
            {var subQ0=sQuery(id+"F0.wireOp",EDGE,"E23");var subQ1=sQuery(id+"F0.wireOp",EDGE,"E10");Q0=makeQuery(id+"F1.opExtrude","SWEPT_EDGE",EDGE,{"disambiguationData":[OSD([subQ1,subQ0]),TDD([makeQuery(id+"F0.imprint","INTERSECT",VERTEX,{"disambiguationData":[OD(0.0)],"derivedFrom":[subQ1,subQ0]})])]});}
            var Q1;
            {var subQ0=sQuery(id+"F0.wireOp",EDGE,"E25");var subQ1=sQuery(id+"F0.wireOp",EDGE,"E10");Q1=makeQuery(id+"F1.opExtrude","SWEPT_EDGE",EDGE,{"disambiguationData":[OSD([subQ1,subQ0]),TDD([makeQuery(id+"F0.imprint","INTERSECT",VERTEX,{"disambiguationData":[OD(0.0)],"derivedFrom":[subQ1,subQ0]})])]});}
            var Q2;
            {var subQ0=sQuery(id+"F0.wireOp",EDGE,"E25");var subQ1=sQuery(id+"F0.wireOp",EDGE,"E9");Q2=makeQuery(id+"F1.opExtrude","SWEPT_EDGE",EDGE,{"disambiguationData":[OSD([subQ1,subQ0]),TDD([makeQuery(id+"F0.imprint","INTERSECT",VERTEX,{"disambiguationData":[OD(0.0)],"derivedFrom":[subQ1,subQ0]})])]});}
            var Q3;
            {var subQ0=sQuery(id+"F0.wireOp",EDGE,"E24");var subQ1=sQuery(id+"F0.wireOp",EDGE,"E9");Q3=makeQuery(id+"F1.opExtrude","SWEPT_EDGE",EDGE,{"disambiguationData":[OSD([subQ1,subQ0]),TDD([makeQuery(id+"F0.imprint","INTERSECT",VERTEX,{"disambiguationData":[OD(0.0)],"derivedFrom":[subQ1,subQ0]})])]});}
            var Q4;
            {var subQ0=sQuery(id+"F0.wireOp",EDGE,"E24");var subQ1=sQuery(id+"F0.wireOp",EDGE,"E8");Q4=makeQuery(id+"F1.opExtrude","SWEPT_EDGE",EDGE,{"disambiguationData":[OSD([subQ1,subQ0]),TDD([makeQuery(id+"F0.imprint","INTERSECT",VERTEX,{"disambiguationData":[OD(0.0)],"derivedFrom":[subQ1,subQ0]})])]});}
            var Q5;
            {var subQ0=sQuery(id+"F0.wireOp",EDGE,"E23");var subQ1=sQuery(id+"F0.wireOp",EDGE,"E8");Q5=makeQuery(id+"F1.opExtrude","SWEPT_EDGE",EDGE,{"disambiguationData":[OSD([subQ1,subQ0]),TDD([makeQuery(id+"F0.imprint","INTERSECT",VERTEX,{"disambiguationData":[OD(0.0)],"derivedFrom":[subQ1,subQ0]})])]});}
            fillet(context, id + "F2", {"entities" : qUnion([Q0, Q1, Q2, Q3, Q4, Q5]), "radius" : 7 * mm, "tangentPropagation" : true, "allowEdgeOverflow" : false});
        }
        {
            var Q0;
            Q0=makeQuery(id+"F1.opExtrude","CAP_EDGE",EDGE,{"disambiguationData":[OSD([sQuery(id+"F0.wireOp",EDGE,"E23")])],"isStart":true});
            var Q1;
            Q1=makeQuery(id+"F1.opExtrude","CAP_EDGE",EDGE,{"disambiguationData":[OSD([sQuery(id+"F0.wireOp",EDGE,"E23")])],"isStart":false});
            fillet(context, id + "F3", {"entities" : qUnion([Q0, Q1]), "radius" : 2 * mm, "tangentPropagation" : true, "allowEdgeOverflow" : false});
        }
    });
